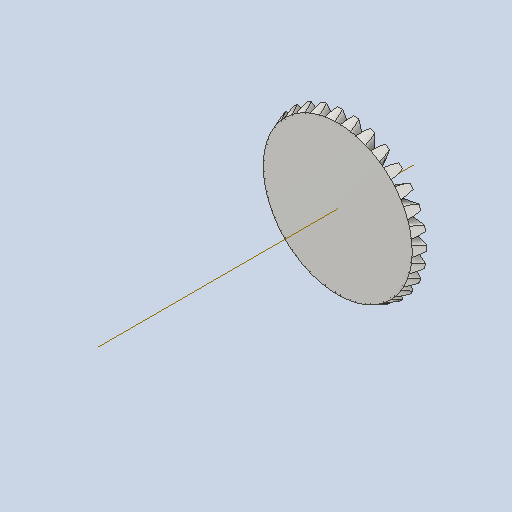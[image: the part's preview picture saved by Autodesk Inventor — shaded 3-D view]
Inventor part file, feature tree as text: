
AUTODESK INVENTOR PART (.ipt)
format: ipt  version: 2022 (Build 260153000, 153)  size: 615,424 bytes
history: native  units: in
note: dims shown in document units (in); Inventor stores cm internally (conversion verified against a paired STEP export)
features: other x30, sketch x1
ambient origin geometry x8: Origin, YZ Plane, XZ Plane, XY Plane, X Axis, Y Axis, Z Axis, Center Point
bodies: Solid1 (feature_tree)
feature tree (31):
  other  "Bevel Gear2"
  other  "Solid1::Bevel Gear2"
  other  "TaggingFeature1"
  other  "Teeth Body Sketch"
  other  "Start Sketch"
  other  "End Sketch"
  other  "End Sketch Right"
  other  "End Sketch Left"
  other  "Body Sketch"
  sketch  "Sketch6"  dims[d0=0.3937in d48=0.0in d49=0.0in d50=90.0deg d52=0.0in d53=0.0in d54=0.0in]
  other  "3D Sketch Right"
  other  "3D Sketch Left"
  other  "Mesh Plane"
  other  "Top Plane"
  other  "Mesh Plane2"
  other  "Tooth Plane"
  other  "End Plane"
  other  "End Plane Right"
  other  "End Plane Left"
  other  "Z Axis_1"
  other  "Top Point"
  other  "Start Point"
  other  "End Point"
  other  "Srf1"
  other  "Srf1::Derived"
  other  "Start plane iMate"
  other  "Mesh iMate2"
  other  "Axis Angle iMate"
  other  "Axis iMate"
  other  "Mesh iMate"
  other  "Intersection iMate"
